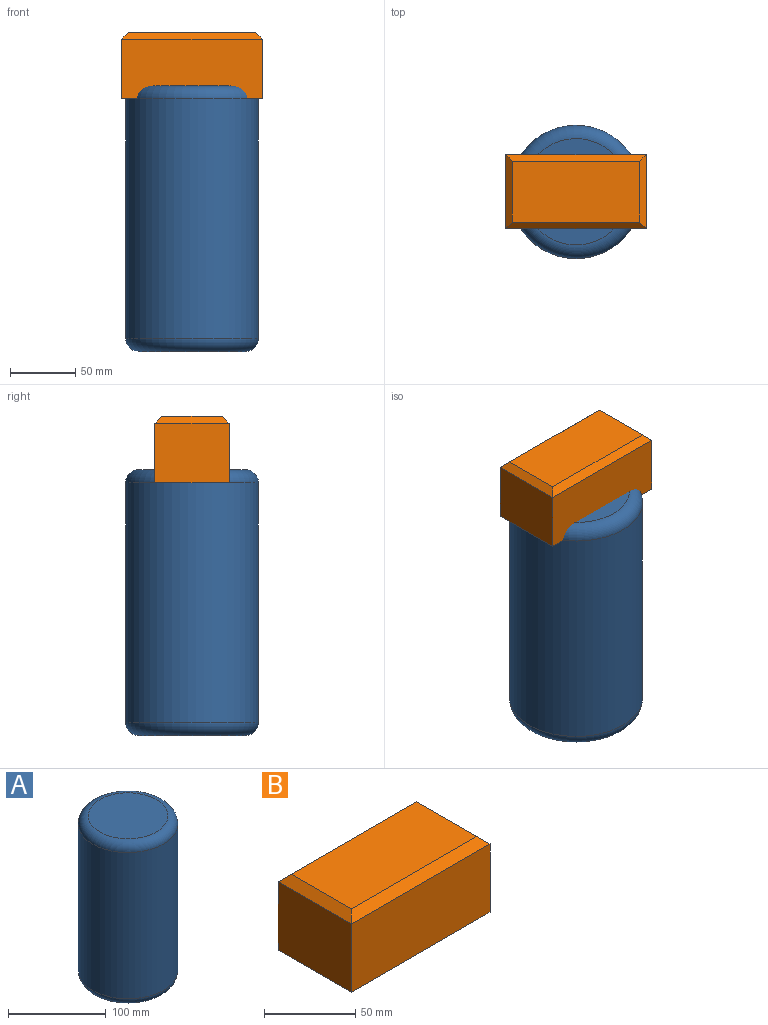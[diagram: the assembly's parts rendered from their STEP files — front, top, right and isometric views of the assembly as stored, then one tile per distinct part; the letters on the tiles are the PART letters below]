
ASSEMBLY  parts=2 mates=1
PART A: 5 faces, bbox 110x110x203.2 mm
  f0: cylinder r=50.8mm len=182.88mm, axis (0,0,-1), area 58372.7mm2, adj f3,f4
  f1: plane 81.28x81.28mm, normal (0,0,1), area 5188.7mm2, adj f4
  f2: plane 81.28x81.28mm, normal (0,0,-1), area 5188.7mm2, adj f3
  f3: torus R=40.64mm, axis (0,0,1), area 4723.8mm2, adj f0,f2
  f4: torus R=40.64mm, axis (0,0,1), area 4723.8mm2, adj f0,f1
PART B: 10 faces, bbox 107.4x56.7x50.8 mm
  f0: plane 107.42x45.72mm, normal (0,-1,0), area 4911.4mm2, adj f1,f3,f5,f8
  f1: plane 56.69x45.72mm, normal (1,0,0), area 2591.7mm2, adj f0,f2,f5,f6
  f2: plane 107.42x45.72mm, normal (0,1,0), area 4911.4mm2, adj f1,f3,f5,f7
  f3: plane 56.69x45.72mm, normal (-1,0,0), area 2591.7mm2, adj f0,f2,f5,f9
  f4: plane 97.26x46.53mm, normal (0,0,1), area 4525.2mm2, adj f6,f7,f8,f9
  f5: plane 107.42x56.69mm, normal (0,0,-1), area 6089.3mm2, adj f0,f1,f2,f3
  f6: plane 56.69x5.08mm, normal (0.71,0,0.71), area 370.7mm2, adj f1,f4,f7,f8
  f7: plane 107.42x5.08mm, normal (0,0.71,0.71), area 735.3mm2, adj f2,f4,f6,f9
  f8: plane 107.42x5.08mm, normal (0,-0.71,0.71), area 735.3mm2, adj f0,f4,f6,f9
  f9: plane 56.69x5.08mm, normal (-0.71,0,0.71), area 370.7mm2, adj f3,f4,f7,f8
PLACE A t=(-100.84,-11.17,-31.03)mm fixed
PLACE B t=(-100.84,-11.17,162.01)mm
MATE planar B.f5 <-> A.f0  axis (0,0,-1) through (-100.84,-11.17,162.01)mm
